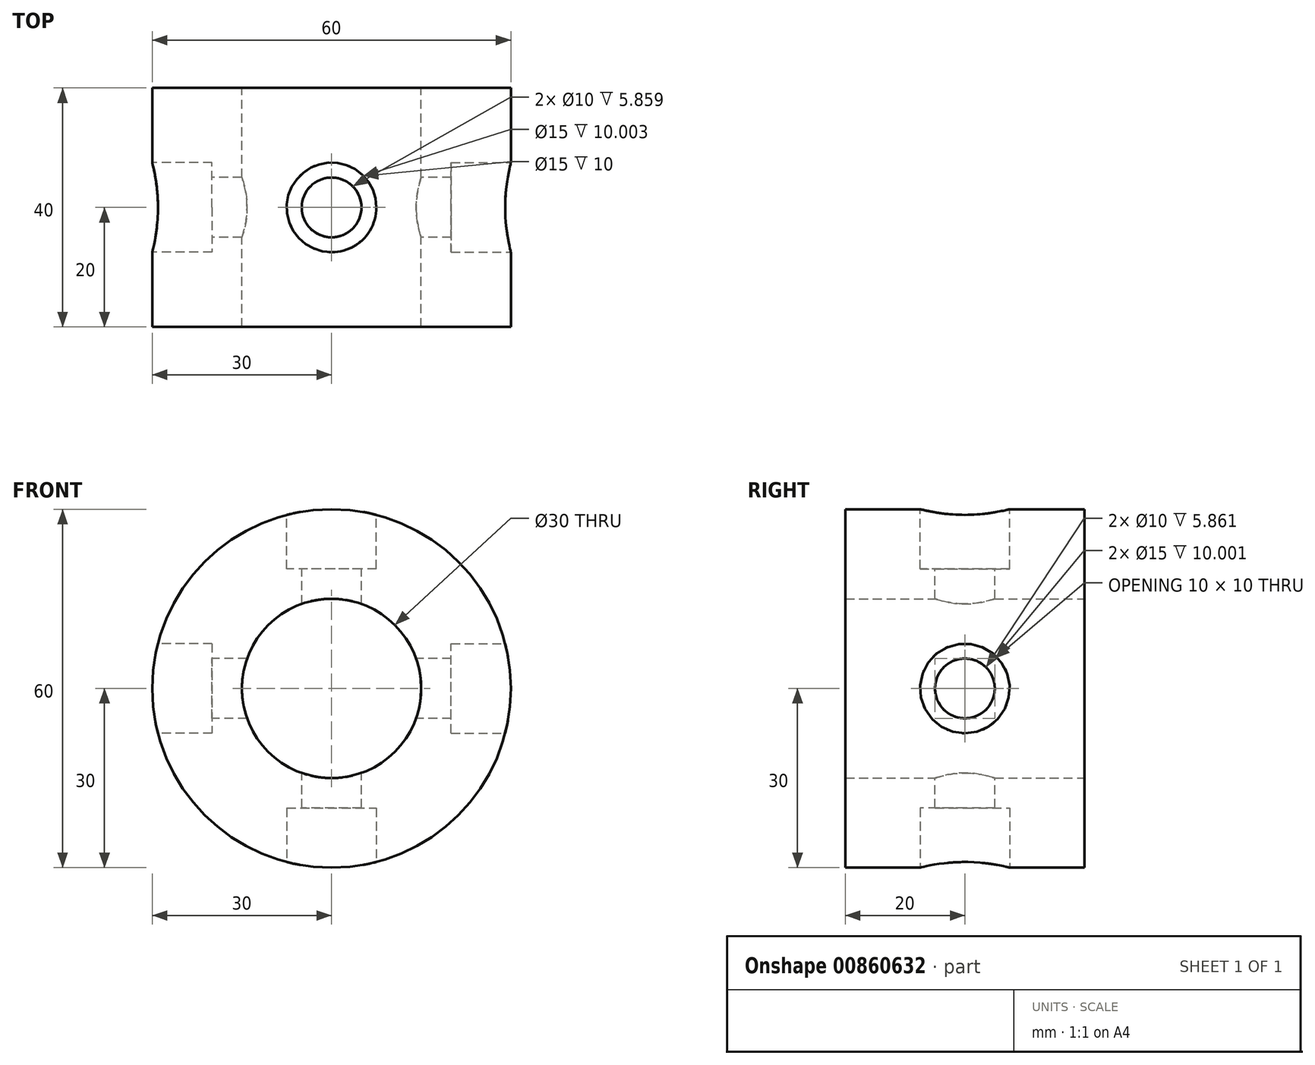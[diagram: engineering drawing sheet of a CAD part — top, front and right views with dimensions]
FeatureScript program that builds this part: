
annotation { "Feature Type Name" : "Feature", "Feature Type Description" : "" }
export const myFeature = defineFeature(function(context is Context, id is Id, definition is map)
    precondition{}
    {
        {
            var Q0;
            Q0=qCreatedBy(makeId("Front.planeOp"),FACE);
            var sketch = newSketch(context, id + "F0", { "sketchPlane" : qUnion([Q0])});
            skCircle(sketch, "E0", {"center": v(0, 0) * mm, "radius": 30 * mm});
            skCircle(sketch, "E1", {"center": v(0, 0) * mm, "radius": 15 * mm});
            skSolve(sketch);
        }
        {
            var Q0;
            Q0=makeQuery(id+"F0.imprint","IMPRINT",FACE,{"disambiguationData":[TD([[makeQuery(id+"F0.imprint","IMPRINT",EDGE,{"derivedFrom":sQuery(id+"F0.wireOp",EDGE,"E0")}),1.0]])]});
            extrude(context, id + "F1", {"entities" : qUnion([Q0]), "endBound" : BoundingType.SYMMETRIC, "depth" : 40 * mm, "offsetDistance" : 25 * mm});
        }
        {
            var Q0;
            Q0=qCreatedBy(makeId("Top.planeOp"),FACE);
            var sketch = newSketch(context, id + "F2", { "sketchPlane" : qUnion([Q0])});
            skCircle(sketch, "E2", {"center": v(0, 0) * mm, "radius": 5 * mm});
            skSolve(sketch);
        }
        {
            var Q0;
            Q0 = qSketchRegion(id + "F2", true);
            extrude(context, id + "F3", {"entities" : qUnion([Q0]), "operationType" : NewBodyOperationType.REMOVE, "endBound" : BoundingType.SYMMETRIC, "oppositeDirection" : true, "depth" : 100.8 * mm, "offsetDistance" : 25 * mm});
        }
        {
            var Q0;
            Q0=qCreatedBy(makeId("Top.planeOp"),FACE);
            cPlane(context, id + "F4", {"entities" : qUnion([Q0]), "cplaneType" : CPlaneType.OFFSET, "offset" : 30 * mm, "width" : 150 * mm, "height" : 150 * mm});
        }
        {
            var Q0;
            Q0=qCreatedBy(makeId("Top.planeOp"),FACE);
            cPlane(context, id + "F5", {"entities" : qUnion([Q0]), "cplaneType" : CPlaneType.OFFSET, "offset" : 30 * mm, "oppositeDirection" : true, "width" : 150 * mm, "height" : 150 * mm});
        }
        {
            var Q0;
            Q0=qCreatedBy(id+"F4.planeOp",FACE);
            var sketch = newSketch(context, id + "F6", { "sketchPlane" : qUnion([Q0])});
            skCircle(sketch, "E3", {"center": v(0, 0) * mm, "radius": 7.5 * mm});
            skSolve(sketch);
        }
        {
            var Q0;
            Q0 = qSketchRegion(id + "F6", true);
            extrude(context, id + "F7", {"entities" : qUnion([Q0]), "operationType" : NewBodyOperationType.REMOVE, "oppositeDirection" : true, "depth" : 10 * mm, "offsetDistance" : 25 * mm});
        }
        {
            var Q0;
            Q0=qCreatedBy(id+"F5.planeOp",FACE);
            var sketch = newSketch(context, id + "F8", { "sketchPlane" : qUnion([Q0])});
            skCircle(sketch, "E4", {"center": v(0, 0) * mm, "radius": 7.5 * mm});
            skSolve(sketch);
        }
        {
            var Q0;
            Q0 = qSketchRegion(id + "F8", true);
            extrude(context, id + "F9", {"entities" : qUnion([Q0]), "operationType" : NewBodyOperationType.REMOVE, "depth" : 10 * mm, "offsetDistance" : 25 * mm});
        }
        {
            var Q0;
            Q0=qCreatedBy(makeId("Right.planeOp"),FACE);
            var sketch = newSketch(context, id + "F10", { "sketchPlane" : qUnion([Q0])});
            skCircle(sketch, "E5", {"center": v(0, 0) * mm, "radius": 5 * mm});
            skSolve(sketch);
        }
        {
            var Q0;
            Q0 = qSketchRegion(id + "F10", true);
            extrude(context, id + "F11", {"entities" : qUnion([Q0]), "operationType" : NewBodyOperationType.REMOVE, "endBound" : BoundingType.SYMMETRIC, "depth" : 89.2 * mm, "offsetDistance" : 25 * mm});
        }
        {
            var Q0;
            Q0=qCreatedBy(makeId("Right.planeOp"),FACE);
            cPlane(context, id + "F12", {"entities" : qUnion([Q0]), "cplaneType" : CPlaneType.OFFSET, "offset" : 30 * mm, "width" : 150 * mm, "height" : 150 * mm});
        }
        {
            var Q0;
            Q0=qCreatedBy(id+"F12.planeOp",FACE);
            var sketch = newSketch(context, id + "F13", { "sketchPlane" : qUnion([Q0])});
            skCircle(sketch, "E6", {"center": v(0, 0) * mm, "radius": 7.5 * mm});
            skSolve(sketch);
        }
        {
            var Q0;
            Q0 = qSketchRegion(id + "F13", true);
            extrude(context, id + "F14", {"entities" : qUnion([Q0]), "operationType" : NewBodyOperationType.REMOVE, "oppositeDirection" : true, "depth" : 10 * mm, "offsetDistance" : 25 * mm});
        }
        {
            var Q0;
            Q0=qCreatedBy(makeId("Right.planeOp"),FACE);
            cPlane(context, id + "F15", {"entities" : qUnion([Q0]), "cplaneType" : CPlaneType.OFFSET, "offset" : 30 * mm, "oppositeDirection" : true, "width" : 150 * mm, "height" : 150 * mm});
        }
        {
            var Q0;
            Q0=qCreatedBy(id+"F15.planeOp",FACE);
            var sketch = newSketch(context, id + "F16", { "sketchPlane" : qUnion([Q0])});
            skCircle(sketch, "E7", {"center": v(0, 0) * mm, "radius": 7.5 * mm});
            skSolve(sketch);
        }
        {
            var Q0;
            Q0 = qSketchRegion(id + "F16", true);
            extrude(context, id + "F17", {"entities" : qUnion([Q0]), "operationType" : NewBodyOperationType.REMOVE, "depth" : 10 * mm, "offsetDistance" : 25 * mm});
        }
    });
